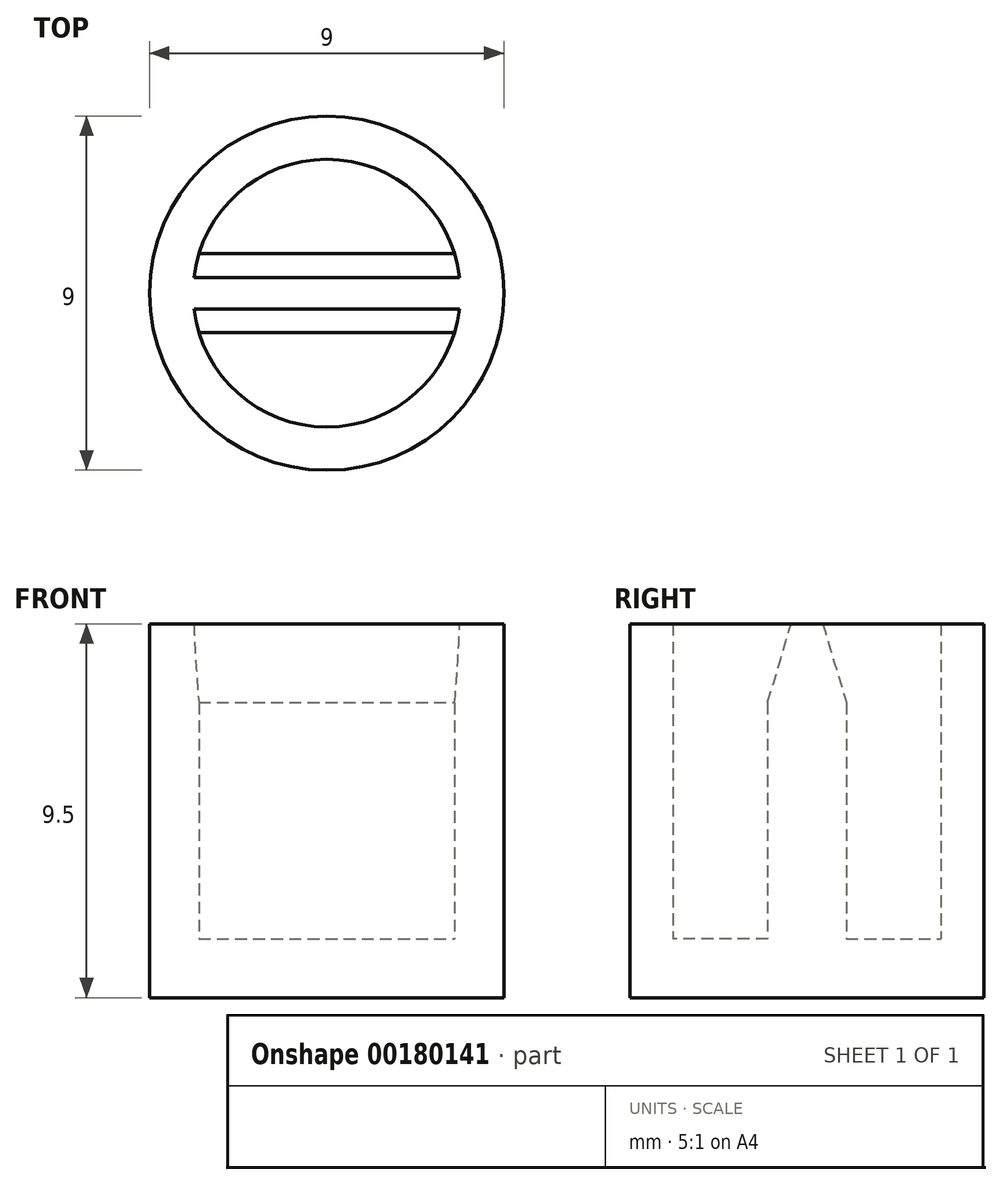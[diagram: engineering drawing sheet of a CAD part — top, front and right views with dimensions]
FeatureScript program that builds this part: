
annotation { "Feature Type Name" : "Feature", "Feature Type Description" : "" }
export const myFeature = defineFeature(function(context is Context, id is Id, definition is map)
    precondition{}
    {
        {
            var Q0;
            Q0=qCreatedBy(makeId("Top.planeOp"),FACE);
            var sketch = newSketch(context, id + "F0", { "sketchPlane" : qUnion([Q0])});
            skCircle(sketch, "E0", {"center": v(0, 0) * mm, "radius": 3.4 * mm});
            skCircle(sketch, "E1", {"center": v(0, 0) * mm, "radius": 4.5 * mm});
            skLineSegment(sketch, "E2", {"start": v(-3.4, 0) * mm, "end": v(3.4, 0) * mm, "construction": true});
            skLineSegment(sketch, "E3", {"start": v(-3.25, 1) * mm, "end": v(3.25, 1) * mm});
            skLineSegment(sketch, "E4.MirrorCS", {"start": v(-3.25, -1) * mm, "end": v(3.25, -1) * mm});
            skSolve(sketch);
        }
        {
            var Q0;
            Q0=makeQuery(id+"F0.imprint","IMPRINT",FACE,{"disambiguationData":[TD([[makeQuery(id+"F0.imprint","IMPRINT",EDGE,{"derivedFrom":sQuery(id+"F0.wireOp",EDGE,"E1")}),1.0]])]});
            var Q1;
            {var subQ0=sQuery(id+"F0.wireOp",EDGE,"E3");Q1=makeQuery(id+"F0.imprint","IMPRINT",FACE,{"disambiguationData":[TD([[makeQuery(id+"F0.imprint","IMPRINT",EDGE,{"derivedFrom":subQ0}),-1.0]])]});}
            extrude(context, id + "F1", {"entities" : qUnion([Q0, Q1]), "depth" : 8 * mm});
        }
        {
            var Q0;
            Q0=makeQuery(id+"F1.opExtrude","CAP_EDGE",EDGE,{"disambiguationData":[OSD([sQuery(id+"F0.wireOp",EDGE,"E3")])],"isStart":false});
            var Q1;
            Q1=makeQuery(id+"F1.opExtrude","CAP_EDGE",EDGE,{"disambiguationData":[OSD([sQuery(id+"F0.wireOp",EDGE,"E4.MirrorCS")])],"isStart":false});
            chamfer(context, id + "F2", {"entities" : qUnion([Q0, Q1]), "chamferType" : ChamferType.TWO_OFFSETS, "width1" : 2 * mm, "oppositeDirection" : false, "width2" : .6 * mm, "tangentPropagation" : true});
        }
        {
            var Q0;
            {var subQ0=sQuery(id+"F0.wireOp",EDGE,"pfCv1kfu-8Ai6-hw5B-6Zcf-5jFLNRCdnBPR");Q0=makeQuery(id+"F0.imprint","IMPRINT",FACE,{"disambiguationData":[TD([[makeQuery(id+"F0.imprint","IMPRINT",EDGE,{"derivedFrom":subQ0}),-1.0]])]});}
            var Q1;
            {var subQ0=sQuery(id+"F0.wireOp",EDGE,"E3");Q1=makeQuery(id+"F0.imprint","IMPRINT",FACE,{"disambiguationData":[TD([[makeQuery(id+"F0.imprint","IMPRINT",EDGE,{"derivedFrom":subQ0}),-1.0]])]});}
            var Q2;
            Q2=makeQuery(id+"F0.imprint","IMPRINT",FACE,{"disambiguationData":[TD([[makeQuery(id+"F0.imprint","IMPRINT",EDGE,{"derivedFrom":sQuery(id+"F0.wireOp",EDGE,"E1")}),1.0]])]});
            var Q3;
            {var subQ0=sQuery(id+"F0.wireOp",EDGE,"E3");Q3=makeQuery(id+"F0.imprint","IMPRINT",FACE,{"disambiguationData":[TD([[makeQuery(id+"F0.imprint","IMPRINT",EDGE,{"derivedFrom":subQ0}),1.0]])]});}
            var Q4;
            {var subQ0=sQuery(id+"F0.wireOp",EDGE,"E4.MirrorCS");Q4=makeQuery(id+"F0.imprint","IMPRINT",FACE,{"disambiguationData":[TD([[makeQuery(id+"F0.imprint","IMPRINT",EDGE,{"derivedFrom":subQ0}),-1.0]])]});}
            extrude(context, id + "F3", {"entities" : qUnion([Q0, Q1, Q2, Q3, Q4]), "operationType" : NewBodyOperationType.ADD, "oppositeDirection" : true, "depth" : 1.5 * mm});
        }
    });
